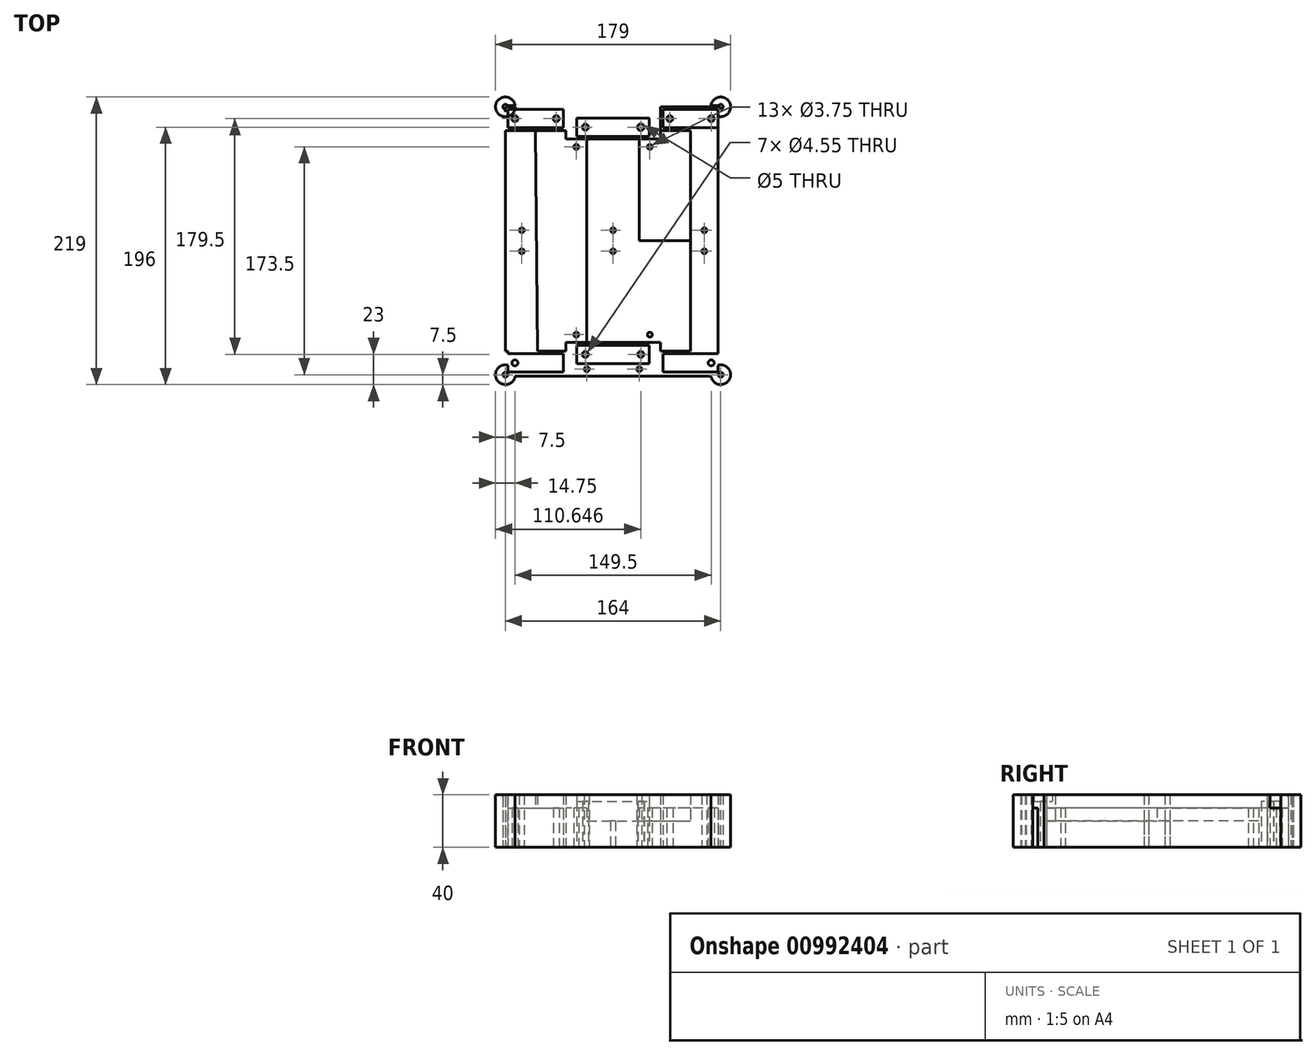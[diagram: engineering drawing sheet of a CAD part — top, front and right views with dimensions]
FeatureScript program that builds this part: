
annotation { "Feature Type Name" : "Feature", "Feature Type Description" : "" }
export const myFeature = defineFeature(function(context is Context, id is Id, definition is map)
    precondition{}
    {
        {
            var Q0;
            Q0=qCreatedBy(makeId("Top.planeOp"),FACE);
            var sketch = newSketch(context, id + "F0", { "sketchPlane" : qUnion([Q0])});
            skLineSegment(sketch, "E0.left", {"start": v(80, -100) * mm, "end": v(80, 100) * mm});
            skLineSegment(sketch, "E0.right", {"start": v(-80, -100) * mm, "end": v(-80, 100) * mm});
            skLineSegment(sketch, "E1.bottom", {"start": v(80, 100) * mm, "end": v(38, 100) * mm});
            skLineSegment(sketch, "E1.top", {"start": v(80, 86) * mm, "end": v(38, 86) * mm});
            skLineSegment(sketch, "E1.left", {"start": v(80, 100) * mm, "end": v(80, 86) * mm});
            skLineSegment(sketch, "E1.right", {"start": v(38, 100) * mm, "end": v(38, 86) * mm});
            skLineSegment(sketch, "E2.bottom", {"start": v(-80, 100) * mm, "end": v(-38, 100) * mm});
            skLineSegment(sketch, "E2.top", {"start": v(-80, 86) * mm, "end": v(-38, 86) * mm});
            skLineSegment(sketch, "E2.left", {"start": v(-80, 100) * mm, "end": v(-80, 86) * mm});
            skLineSegment(sketch, "E2.right", {"start": v(-38, 100) * mm, "end": v(-38, 86) * mm});
            skLineSegment(sketch, "E3.bottom", {"start": v(-27.6, 93.5) * mm, "end": v(27.65, 93.5) * mm});
            skLineSegment(sketch, "E3.top", {"start": v(-27.6, 79.5) * mm, "end": v(27.65, 79.5) * mm});
            skLineSegment(sketch, "E3.left", {"start": v(-27.6, 93.5) * mm, "end": v(-27.6, 79.5) * mm});
            skLineSegment(sketch, "E3.right", {"start": v(27.65, 93.5) * mm, "end": v(27.65, 79.5) * mm});
            skCircle(sketch, "E4", {"center": v(43.25, 93) * mm, "radius": 2.27 * mm});
            skPoint(sketch, "E4.centerSnap0", {"position": v(38, 93) * mm});
            skCircle(sketch, "E5", {"center": v(74.75, 93) * mm, "radius": 2.27 * mm});
            skCircle(sketch, "E6", {"center": v(-43.25, 93) * mm, "radius": 2.27 * mm});
            skPoint(sketch, "E6.centerSnap0", {"position": v(-38, 93) * mm});
            skCircle(sketch, "E7", {"center": v(-74.75, 93) * mm, "radius": 2.27 * mm});
            skPoint(sketch, "E7.centerSnap0", {"position": v(-80, 93) * mm});
            skCircle(sketch, "E8", {"center": v(-21.1, 86.5) * mm, "radius": 2.27 * mm});
            skPoint(sketch, "E8.centerSnap0", {"position": v(-27.6, 86.5) * mm});
            skCircle(sketch, "E9", {"center": v(21.15, 86.5) * mm, "radius": 2.5 * mm});
            skPoint(sketch, "E9.centerSnap0", {"position": v(27.65, 86.5) * mm});
            skLineSegment(sketch, "E10.2", {"start": v(-20, 77.5) * mm, "end": v(20, 77.5) * mm});
            skLineSegment(sketch, "E11.0", {"start": v(82, 102) * mm, "end": v(-82, 102) * mm});
            skLineSegment(sketch, "E11.1", {"start": v(82, -102) * mm, "end": v(82, 102) * mm});
            skLineSegment(sketch, "E11.3", {"start": v(-82, -102.02) * mm, "end": v(-82, 102) * mm});
            skLineSegment(sketch, "E12.0", {"start": v(-82, 84) * mm, "end": v(-36, 84) * mm});
            skLineSegment(sketch, "E12.1", {"start": v(-36, 102) * mm, "end": v(-36, 84) * mm});
            skLineSegment(sketch, "E13.0", {"start": v(82, 84) * mm, "end": v(36, 84) * mm});
            skLineSegment(sketch, "E13.1", {"start": v(36, 102) * mm, "end": v(36, 84) * mm});
            skLineSegment(sketch, "E14", {"start": v(-59, 84) * mm, "end": v(-57.51, -84) * mm});
            skLineSegment(sketch, "E15", {"start": v(59, 84) * mm, "end": v(59, -84) * mm});
            skLineSegment(sketch, "E16", {"start": v(82, 0) * mm, "end": v(80, 0) * mm});
            skLineSegment(sketch, "E17", {"start": v(80, 0) * mm, "end": v(59, 0) * mm});
            skLineSegment(sketch, "E18", {"start": v(59, 0) * mm, "end": v(0, 0) * mm});
            skLineSegment(sketch, "E19", {"start": v(0, 0) * mm, "end": v(-20, 0) * mm});
            skLineSegment(sketch, "E20", {"start": v(-58.26, 0) * mm, "end": v(-80, 0) * mm});
            skLineSegment(sketch, "E21.MirrorCS", {"start": v(-27.6, -93.5) * mm, "end": v(-27.6, -79.5) * mm});
            skCircle(sketch, "E22.MirrorC", {"center": v(-21.1, -86.5) * mm, "radius": 2.27 * mm});
            skCircle(sketch, "E23.MirrorC", {"center": v(74.75, -93) * mm, "radius": 2.27 * mm});
            skCircle(sketch, "E24.MirrorC", {"center": v(-74.75, -93) * mm, "radius": 2.27 * mm});
            skLineSegment(sketch, "E25.MirrorCS", {"start": v(-38, -100) * mm, "end": v(-38, -86) * mm});
            skLineSegment(sketch, "E26.MirrorCS", {"start": v(-36, -102) * mm, "end": v(-36, -84) * mm});
            skCircle(sketch, "E27.MirrorC", {"center": v(43.25, -93) * mm, "radius": 2.27 * mm});
            skCircle(sketch, "E28.MirrorC", {"center": v(21.15, -86.5) * mm, "radius": 2.27 * mm});
            skCircle(sketch, "E29.MirrorC", {"center": v(-43.25, -93) * mm, "radius": 2.27 * mm});
            skLineSegment(sketch, "E30.MirrorCS", {"start": v(27.65, -93.5) * mm, "end": v(27.65, -79.5) * mm});
            skLineSegment(sketch, "E31.MirrorCS", {"start": v(38, -100) * mm, "end": v(38, -86) * mm});
            skPoint(sketch, "E32.MirrorP", {"position": v(-38, -93) * mm});
            skLineSegment(sketch, "E33.MirrorCS", {"start": v(36, -102) * mm, "end": v(36, -84) * mm});
            skLineSegment(sketch, "E34.MirrorCS", {"start": v(80, -100) * mm, "end": v(80, -86) * mm});
            skPoint(sketch, "E35.MirrorP", {"position": v(-27.6, -86.5) * mm});
            skLineSegment(sketch, "E36.MirrorCS", {"start": v(-80, -100) * mm, "end": v(-80, -86) * mm});
            skLineSegment(sketch, "E37.MirrorCS", {"start": v(-82, -84) * mm, "end": v(-36, -84) * mm});
            skLineSegment(sketch, "E38.MirrorCS", {"start": v(-80, -86) * mm, "end": v(-38, -86) * mm});
            skPoint(sketch, "E39.MirrorP", {"position": v(38, -93) * mm});
            skLineSegment(sketch, "E40.MirrorCS", {"start": v(80, -86) * mm, "end": v(38, -86) * mm});
            skLineSegment(sketch, "E41.MirrorCS", {"start": v(-27.6, -79.5) * mm, "end": v(27.65, -79.5) * mm});
            skLineSegment(sketch, "E42.MirrorCS", {"start": v(82, -102.97) * mm, "end": v(-82, -102.97) * mm});
            skLineSegment(sketch, "E43.MirrorCS", {"start": v(82, -84) * mm, "end": v(36, -84) * mm});
            skPoint(sketch, "E44.MirrorP", {"position": v(27.65, -86.5) * mm});
            skLineSegment(sketch, "E45.MirrorCS", {"start": v(-27.6, -93.5) * mm, "end": v(27.65, -93.5) * mm});
            skLineSegment(sketch, "E46.MirrorCS", {"start": v(80, -100) * mm, "end": v(38, -100) * mm});
            skPoint(sketch, "E47.MirrorP", {"position": v(-80, -93) * mm});
            skLineSegment(sketch, "E48.MirrorCS", {"start": v(-80, -100) * mm, "end": v(-38, -100) * mm});
            skPoint(sketch, "E49", {"position": v(-80, 0) * mm});
            skPoint(sketch, "E50", {"position": v(-82, 0) * mm});
            skPoint(sketch, "E51", {"position": v(-80, 84) * mm});
            skPoint(sketch, "E52", {"position": v(-82, 84) * mm});
            skPoint(sketch, "E53", {"position": v(80, 84) * mm});
            skPoint(sketch, "E54", {"position": v(82, 84) * mm});
            skPoint(sketch, "E55", {"position": v(80, 0) * mm});
            skPoint(sketch, "E56", {"position": v(82, 0) * mm});
            skLineSegment(sketch, "E57", {"start": v(-82, 84) * mm, "end": v(-80, 84) * mm});
            skLineSegment(sketch, "E58", {"start": v(80, 84) * mm, "end": v(82, 84) * mm});
            skLineSegment(sketch, "E59", {"start": v(36, 102) * mm, "end": v(36, 100) * mm});
            skLineSegment(sketch, "E60", {"start": v(-82, 0) * mm, "end": v(-80, 0) * mm});
            skLineSegment(sketch, "E61", {"start": v(-82, -84) * mm, "end": v(-80, -84) * mm});
            skLineSegment(sketch, "E62", {"start": v(80, -84) * mm, "end": v(82, -84) * mm});
            skLineSegment(sketch, "E63", {"start": v(80, 0) * mm, "end": v(82, 0) * mm});
            skLineSegment(sketch, "E64", {"start": v(-38, 100) * mm, "end": v(-80, 100) * mm});
            skLineSegment(sketch, "E65", {"start": v(-57.51, -84) * mm, "end": v(-58.26, 0) * mm});
            skLineSegment(sketch, "E66", {"start": v(-58.26, 0) * mm, "end": v(-20, 0) * mm});
            skCircle(sketch, "E67.MirrorC", {"center": v(21.15, 86.5) * mm, "radius": 2.27 * mm});
            skLineSegment(sketch, "E68.MirrorCS", {"start": v(82, 102.97) * mm, "end": v(-82, 102.97) * mm});
            skLineSegment(sketch, "E69", {"start": v(36, -102) * mm, "end": v(36, -77.5) * mm});
            skLineSegment(sketch, "E70", {"start": v(-36, -102) * mm, "end": v(-36, -77.5) * mm});
            skLineSegment(sketch, "E71", {"start": v(36, -77.5) * mm, "end": v(-36, -77.5) * mm});
            skLineSegment(sketch, "E72", {"start": v(20, -77.5) * mm, "end": v(20, 77.5) * mm});
            skLineSegment(sketch, "E73", {"start": v(-20, 77.5) * mm, "end": v(-20, -77.5) * mm});
            skLineSegment(sketch, "E74", {"start": v(36, 84) * mm, "end": v(36, 77.5) * mm});
            skLineSegment(sketch, "E75", {"start": v(36, 77.5) * mm, "end": v(20, 77.5) * mm});
            skLineSegment(sketch, "E76", {"start": v(-36, 84) * mm, "end": v(-36, 77.5) * mm});
            skLineSegment(sketch, "E77", {"start": v(-20, 77.5) * mm, "end": v(-36, 77.5) * mm});
            skLineSegment(sketch, "E78.bottom", {"start": v(-36, 102) * mm, "end": v(36, 102) * mm});
            skLineSegment(sketch, "E78.top", {"start": v(-36, 172) * mm, "end": v(36, 172) * mm});
            skLineSegment(sketch, "E78.left", {"start": v(-36, 102) * mm, "end": v(-36, 172) * mm});
            skLineSegment(sketch, "E78.right", {"start": v(36, 102) * mm, "end": v(36, 172) * mm});
            skLineSegment(sketch, "E79", {"start": v(0, 102) * mm, "end": v(0, 172) * mm});
            skCircle(sketch, "E80", {"center": v(-15, 127) * mm, "radius": 2 * mm});
            skCircle(sketch, "E81", {"center": v(-15, 152.4) * mm, "radius": 2 * mm});
            skCircle(sketch, "E82.MirrorC", {"center": v(15, 127) * mm, "radius": 2 * mm});
            skCircle(sketch, "E83.MirrorC", {"center": v(15, 152.4) * mm, "radius": 2 * mm});
            skLineSegment(sketch, "E84", {"start": v(-33.47, 102) * mm, "end": v(-33.47, 98) * mm});
            skLineSegment(sketch, "E85", {"start": v(-33.47, 98) * mm, "end": v(-29.47, 98) * mm});
            skLineSegment(sketch, "E86", {"start": v(-29.47, 98) * mm, "end": v(-29.47, 100) * mm});
            skLineSegment(sketch, "E87", {"start": v(-29.47, 100) * mm, "end": v(-31.47, 100) * mm});
            skLineSegment(sketch, "E88", {"start": v(-31.47, 100) * mm, "end": v(-31.47, 102) * mm});
            skLineSegment(sketch, "E89.0", {"start": v(-31.27, 100.2) * mm, "end": v(-31.27, 102) * mm});
            skLineSegment(sketch, "E89.1", {"start": v(-33.67, 102) * mm, "end": v(-33.67, 97.8) * mm});
            skLineSegment(sketch, "E89.2", {"start": v(-33.67, 97.8) * mm, "end": v(-29.27, 97.8) * mm});
            skLineSegment(sketch, "E89.3", {"start": v(-29.27, 97.8) * mm, "end": v(-29.27, 100.2) * mm});
            skLineSegment(sketch, "E89.4", {"start": v(-29.27, 100.2) * mm, "end": v(-31.27, 100.2) * mm});
            skLineSegment(sketch, "E90.MirrorCS", {"start": v(31.27, 100.2) * mm, "end": v(31.27, 102) * mm});
            skLineSegment(sketch, "E91.MirrorCS", {"start": v(31.47, 100) * mm, "end": v(31.47, 102) * mm});
            skLineSegment(sketch, "E92.MirrorCS", {"start": v(33.47, 102) * mm, "end": v(33.47, 98) * mm});
            skLineSegment(sketch, "E93.MirrorCS", {"start": v(33.67, 102) * mm, "end": v(33.67, 97.8) * mm});
            skLineSegment(sketch, "E94.MirrorCS", {"start": v(29.27, 97.8) * mm, "end": v(29.27, 100.2) * mm});
            skLineSegment(sketch, "E95.MirrorCS", {"start": v(29.47, 100) * mm, "end": v(31.47, 100) * mm});
            skLineSegment(sketch, "E96.MirrorCS", {"start": v(33.67, 97.8) * mm, "end": v(29.27, 97.8) * mm});
            skLineSegment(sketch, "E97.MirrorCS", {"start": v(29.47, 98) * mm, "end": v(29.47, 100) * mm});
            skLineSegment(sketch, "E98.MirrorCS", {"start": v(29.27, 100.2) * mm, "end": v(31.27, 100.2) * mm});
            skLineSegment(sketch, "E99.MirrorCS", {"start": v(33.47, 98) * mm, "end": v(29.47, 98) * mm});
            skLineSegment(sketch, "E100", {"start": v(-39.13, 0) * mm, "end": v(-39.13, -2.14) * mm});
            skLineSegment(sketch, "E101", {"start": v(-39.13, -2.14) * mm, "end": v(-37.13, -2.14) * mm});
            skLineSegment(sketch, "E102", {"start": v(-37.13, -2.14) * mm, "end": v(-37.13, -4.14) * mm});
            skLineSegment(sketch, "E103", {"start": v(-37.13, -4.14) * mm, "end": v(-43.13, -4.14) * mm});
            skLineSegment(sketch, "E104", {"start": v(-43.13, -4.14) * mm, "end": v(-43.13, -2.14) * mm});
            skLineSegment(sketch, "E105", {"start": v(-43.13, -2.14) * mm, "end": v(-41.13, -2.15) * mm});
            skLineSegment(sketch, "E106", {"start": v(-41.13, -2.15) * mm, "end": v(-41.13, 0) * mm});
            skLineSegment(sketch, "E107.0", {"start": v(-41.38, -1.9) * mm, "end": v(-41.38, 0) * mm});
            skLineSegment(sketch, "E107.1", {"start": v(-43.38, -1.89) * mm, "end": v(-41.38, -1.9) * mm});
            skLineSegment(sketch, "E107.2", {"start": v(-43.38, -4.39) * mm, "end": v(-43.38, -1.89) * mm});
            skLineSegment(sketch, "E107.3", {"start": v(-38.88, 0) * mm, "end": v(-38.88, -1.89) * mm});
            skLineSegment(sketch, "E107.4", {"start": v(-38.88, -1.89) * mm, "end": v(-36.88, -1.89) * mm});
            skLineSegment(sketch, "E107.5", {"start": v(-36.88, -1.89) * mm, "end": v(-36.88, -4.39) * mm});
            skLineSegment(sketch, "E107.6", {"start": v(-36.88, -4.39) * mm, "end": v(-43.38, -4.39) * mm});
            skLineSegment(sketch, "E108.MirrorCS", {"start": v(43.13, -2.14) * mm, "end": v(41.13, -2.15) * mm});
            skLineSegment(sketch, "E109.MirrorCS", {"start": v(39.13, -2.14) * mm, "end": v(37.13, -2.14) * mm});
            skLineSegment(sketch, "E110.MirrorCS", {"start": v(36.88, -4.39) * mm, "end": v(43.38, -4.39) * mm});
            skLineSegment(sketch, "E111.MirrorCS", {"start": v(43.38, -1.89) * mm, "end": v(41.38, -1.9) * mm});
            skLineSegment(sketch, "E112.MirrorCS", {"start": v(37.13, -4.14) * mm, "end": v(43.13, -4.14) * mm});
            skLineSegment(sketch, "E113.MirrorCS", {"start": v(36.88, -1.89) * mm, "end": v(36.88, -4.39) * mm});
            skLineSegment(sketch, "E114.MirrorCS", {"start": v(43.38, -4.39) * mm, "end": v(43.38, -1.89) * mm});
            skLineSegment(sketch, "E115.MirrorCS", {"start": v(38.88, -1.89) * mm, "end": v(36.88, -1.89) * mm});
            skLineSegment(sketch, "E116.MirrorCS", {"start": v(43.13, -4.14) * mm, "end": v(43.13, -2.14) * mm});
            skLineSegment(sketch, "E117.MirrorCS", {"start": v(37.13, -2.14) * mm, "end": v(37.13, -4.14) * mm});
            skLineSegment(sketch, "E118.MirrorCS", {"start": v(41.38, -1.9) * mm, "end": v(41.38, 0) * mm});
            skLineSegment(sketch, "E119.MirrorCS", {"start": v(41.13, -2.15) * mm, "end": v(41.13, 0) * mm});
            skLineSegment(sketch, "E120.MirrorCS", {"start": v(39.13, 0) * mm, "end": v(39.13, -2.14) * mm});
            skLineSegment(sketch, "E121.MirrorCS", {"start": v(38.88, 0) * mm, "end": v(38.88, -1.89) * mm});
            skLineSegment(sketch, "E122.MirrorCS", {"start": v(-29.27, -100.2) * mm, "end": v(-31.27, -100.2) * mm});
            skLineSegment(sketch, "E123.MirrorCS", {"start": v(-29.27, -97.8) * mm, "end": v(-29.27, -100.2) * mm});
            skLineSegment(sketch, "E124.MirrorCS", {"start": v(-33.47, -98) * mm, "end": v(-29.47, -98) * mm});
            skLineSegment(sketch, "E125.MirrorCS", {"start": v(-29.47, -100) * mm, "end": v(-31.47, -100) * mm});
            skLineSegment(sketch, "E126.MirrorCS", {"start": v(-29.47, -98) * mm, "end": v(-29.47, -100) * mm});
            skLineSegment(sketch, "E127.MirrorCS", {"start": v(-33.67, -97.8) * mm, "end": v(-29.27, -97.8) * mm});
            skLineSegment(sketch, "E128.MirrorCS", {"start": v(-33.67, -102) * mm, "end": v(-33.67, -97.8) * mm});
            skLineSegment(sketch, "E129.MirrorCS", {"start": v(-33.47, -102) * mm, "end": v(-33.47, -98) * mm});
            skLineSegment(sketch, "E130.MirrorCS", {"start": v(-31.47, -100) * mm, "end": v(-31.47, -102) * mm});
            skLineSegment(sketch, "E131.MirrorCS", {"start": v(-31.27, -100.2) * mm, "end": v(-31.27, -102) * mm});
            skLineSegment(sketch, "E132.MirrorCS", {"start": v(29.27, -97.8) * mm, "end": v(29.27, -100.2) * mm});
            skLineSegment(sketch, "E133.MirrorCS", {"start": v(29.27, -100.2) * mm, "end": v(31.27, -100.2) * mm});
            skLineSegment(sketch, "E134.MirrorCS", {"start": v(29.47, -98) * mm, "end": v(29.47, -100) * mm});
            skLineSegment(sketch, "E135.MirrorCS", {"start": v(29.47, -100) * mm, "end": v(31.47, -100) * mm});
            skLineSegment(sketch, "E136.MirrorCS", {"start": v(33.67, -97.8) * mm, "end": v(29.27, -97.8) * mm});
            skLineSegment(sketch, "E137.MirrorCS", {"start": v(33.47, -98) * mm, "end": v(29.47, -98) * mm});
            skLineSegment(sketch, "E138.MirrorCS", {"start": v(33.47, -102) * mm, "end": v(33.47, -98) * mm});
            skLineSegment(sketch, "E139.MirrorCS", {"start": v(33.67, -102) * mm, "end": v(33.67, -97.8) * mm});
            skLineSegment(sketch, "E140.MirrorCS", {"start": v(31.47, -100) * mm, "end": v(31.47, -102) * mm});
            skLineSegment(sketch, "E141.MirrorCS", {"start": v(31.27, -100.2) * mm, "end": v(31.27, -102) * mm});
            skCircle(sketch, "E142", {"center": v(36, 172) * mm, "radius": 7.5 * mm});
            skCircle(sketch, "E143.MirrorC", {"center": v(-36, 172) * mm, "radius": 7.5 * mm});
            skCircle(sketch, "E144", {"center": v(82, 102) * mm, "radius": 7.5 * mm});
            skCircle(sketch, "E145", {"center": v(82, -102) * mm, "radius": 7.5 * mm});
            skCircle(sketch, "E146", {"center": v(82, -102) * mm, "radius": 1.88 * mm});
            skCircle(sketch, "E147", {"center": v(82, 102) * mm, "radius": 1.88 * mm});
            skCircle(sketch, "E148", {"center": v(36, 172) * mm, "radius": 1.88 * mm});
            skCircle(sketch, "E149.MirrorC", {"center": v(-36, 172) * mm, "radius": 1.88 * mm});
            skCircle(sketch, "E150.MirrorC", {"center": v(-82, 102) * mm, "radius": 1.88 * mm});
            skCircle(sketch, "E151.MirrorC", {"center": v(-82, 102) * mm, "radius": 7.5 * mm});
            skCircle(sketch, "E152.MirrorC", {"center": v(-82, -102) * mm, "radius": 1.88 * mm});
            skCircle(sketch, "E153.MirrorC", {"center": v(-82, -102) * mm, "radius": 7.5 * mm});
            skCircle(sketch, "E154", {"center": v(24, 108) * mm, "radius": 1.88 * mm});
            skCircle(sketch, "E155.MirrorC", {"center": v(-24, 108) * mm, "radius": 1.88 * mm});
            skCircle(sketch, "E156", {"center": v(20, 97.8) * mm, "radius": 1.88 * mm});
            skLineSegment(sketch, "E157", {"start": v(0, 102) * mm, "end": v(0, 93.5) * mm});
            skPoint(sketch, "E158", {"position": v(0, 97.75) * mm});
            skCircle(sketch, "E159.MirrorC", {"center": v(-20, 97.8) * mm, "radius": 1.88 * mm});
            skCircle(sketch, "E160.MirrorC", {"center": v(-20, -97.8) * mm, "radius": 1.88 * mm});
            skCircle(sketch, "E161.MirrorC", {"center": v(20, -97.8) * mm, "radius": 1.88 * mm});
            skCircle(sketch, "E162", {"center": v(0, -8) * mm, "radius": 1.88 * mm});
            skCircle(sketch, "E163", {"center": v(69.5, -8) * mm, "radius": 1.88 * mm});
            skPoint(sketch, "E163.centerSnap0", {"position": v(69.5, 0) * mm});
            skCircle(sketch, "E164.MirrorC", {"center": v(-69.5, -8) * mm, "radius": 1.88 * mm});
            skCircle(sketch, "E165.MirrorC", {"center": v(-69.5, 8) * mm, "radius": 1.88 * mm});
            skCircle(sketch, "E166.MirrorC", {"center": v(0, 8) * mm, "radius": 1.88 * mm});
            skCircle(sketch, "E167.MirrorC", {"center": v(69.5, 8) * mm, "radius": 1.88 * mm});
            skCircle(sketch, "E168", {"center": v(28, 71.5) * mm, "radius": 1.88 * mm});
            skCircle(sketch, "E169.MirrorC", {"center": v(-28, 71.5) * mm, "radius": 1.88 * mm});
            skCircle(sketch, "E170.MirrorC", {"center": v(28, -71.5) * mm, "radius": 1.88 * mm});
            skCircle(sketch, "E171.MirrorC", {"center": v(-28, -71.5) * mm, "radius": 1.88 * mm});
            skPoint(sketch, "E172", {"position": v(0, -102.97) * mm});
            skLineSegment(sketch, "E173", {"start": v(0, -102.97) * mm, "end": v(0, -166.97) * mm});
            skLineSegment(sketch, "E174.bottom", {"start": v(59.56, -102.97) * mm, "end": v(-59.56, -102.97) * mm});
            skPoint(sketch, "E174.middle", {"position": v(0, -166.97) * mm});
            skLineSegment(sketch, "E175", {"start": v(-59.56, -166.97) * mm, "end": v(59.56, -166.97) * mm});
            skLineSegment(sketch, "E176.0", {"start": v(-59.56, -162.97) * mm, "end": v(59.56, -162.97) * mm});
            skLineSegment(sketch, "E177", {"start": v(-59.56, -102.97) * mm, "end": v(-59.56, -166.97) * mm});
            skLineSegment(sketch, "E178", {"start": v(59.56, -102.97) * mm, "end": v(59.56, -166.97) * mm});
            skLineSegment(sketch, "E179", {"start": v(-59.56, -166.97) * mm, "end": v(-59.56, -316.97) * mm});
            skLineSegment(sketch, "E180", {"start": v(-59.56, -316.97) * mm, "end": v(59.56, -316.97) * mm});
            skLineSegment(sketch, "E181", {"start": v(59.56, -316.97) * mm, "end": v(59.56, -166.97) * mm});
            skSolve(sketch);
        }
        {
            var Q0;
            {var subQ4=sQuery(id+"F0.wireOp",EDGE,"E14");Q0=makeQuery(id+"F0.imprint","IMPRINT",FACE,{"disambiguationData":[TD([[makeQuery(id+"F0.imprint","IMPRINT",EDGE,{"derivedFrom":subQ4}),-1.0]])]});}
            var Q1;
            {var subQ4=sQuery(id+"F0.wireOp",EDGE,"E19");Q1=makeQuery(id+"F0.imprint","IMPRINT",FACE,{"disambiguationData":[TD([[makeQuery(id+"F0.imprint","IMPRINT",EDGE,{"derivedFrom":subQ4}),-1.0]])]});}
            var Q2;
            Q2=makeQuery(id+"F0.imprint","IMPRINT",FACE,{"disambiguationData":[TD([[makeQuery(id+"F0.imprint","IMPRINT",EDGE,{"derivedFrom":sQuery(id+"F0.wireOp",EDGE,"E21.MirrorCS")}),-1.0]])]});
            var Q3;
            Q3=makeQuery(id+"F0.imprint","IMPRINT",FACE,{"disambiguationData":[TD([[makeQuery(id+"F0.imprint","IMPRINT",EDGE,{"derivedFrom":sQuery(id+"F0.wireOp",EDGE,"E23.MirrorC")}),1.0]])]});
            var Q4;
            {var subQ6=sQuery(id+"F0.wireOp",EDGE,"E74");Q4=makeQuery(id+"F0.imprint","IMPRINT",FACE,{"disambiguationData":[TD([[makeQuery(id+"F0.imprint","IMPRINT",EDGE,{"derivedFrom":subQ6}),1.0]])]});}
            var Q5;
            Q5=makeQuery(id+"F0.imprint","IMPRINT",FACE,{"disambiguationData":[TD([[makeQuery(id+"F0.imprint","IMPRINT",EDGE,{"derivedFrom":sQuery(id+"F0.wireOp",EDGE,"E24.MirrorC")}),1.0]])]});
            var Q6;
            {var subQ1=sQuery(id+"F0.wireOp",EDGE,"E43.MirrorCS");var subQ6=sQuery(id+"F0.wireOp",EDGE,"E15");var subQ10=makeQuery(id+"F0.imprint","INTERSECT",VERTEX,{"derivedFrom":[subQ6,subQ1]});Q6=makeQuery(id+"F0.imprint","IMPRINT",FACE,{"disambiguationData":[TD([[makeQuery(id+"F0.imprint","IMPRINT",EDGE,{"disambiguationData":[TD([[subQ10,-1.0]])],"derivedFrom":subQ1}),-1.0]])]});}
            var Q7;
            Q7=makeQuery(id+"F0.imprint","IMPRINT",FACE,{"disambiguationData":[TD([[makeQuery(id+"F0.imprint","IMPRINT",EDGE,{"derivedFrom":sQuery(id+"F0.wireOp",EDGE,"E7")}),-1.0]])]});
            var Q8;
            {var subQ7=sQuery(id+"F0.wireOp",EDGE,"E19");Q8=makeQuery(id+"F0.imprint","IMPRINT",FACE,{"disambiguationData":[TD([[makeQuery(id+"F0.imprint","IMPRINT",EDGE,{"derivedFrom":subQ7}),1.0]])]});}
            var Q9;
            Q9=makeQuery(id+"F0.imprint","IMPRINT",FACE,{"disambiguationData":[TD([[makeQuery(id+"F0.imprint","IMPRINT",EDGE,{"derivedFrom":sQuery(id+"F0.wireOp",EDGE,"E1.right")}),1.0]])]});
            var Q10;
            {var subQ6=sQuery(id+"F0.wireOp",EDGE,"E65");Q10=makeQuery(id+"F0.imprint","IMPRINT",FACE,{"disambiguationData":[TD([[makeQuery(id+"F0.imprint","IMPRINT",EDGE,{"derivedFrom":subQ6}),-1.0]])]});}
            var Q11;
            Q11=makeQuery(id+"F0.imprint","IMPRINT",FACE,{"disambiguationData":[TD([[makeQuery(id+"F0.imprint","IMPRINT",EDGE,{"derivedFrom":sQuery(id+"F0.wireOp",EDGE,"E8")}),-1.0]])]});
            var Q12;
            {var subQ1=sQuery(id+"F0.wireOp",EDGE,"E14");Q12=makeQuery(id+"F0.imprint","IMPRINT",FACE,{"disambiguationData":[TD([[makeQuery(id+"F0.imprint","IMPRINT",EDGE,{"derivedFrom":subQ1}),1.0]])]});}
            var Q13;
            {var subQ0=sQuery(id+"F0.wireOp",EDGE,"E17");Q13=makeQuery(id+"F0.imprint","IMPRINT",FACE,{"disambiguationData":[TD([[makeQuery(id+"F0.imprint","IMPRINT",EDGE,{"derivedFrom":subQ0}),1.0]])]});}
            var Q14;
            Q14=makeQuery(id+"F0.imprint","IMPRINT",FACE,{"disambiguationData":[TD([[makeQuery(id+"F0.imprint","IMPRINT",EDGE,{"derivedFrom":sQuery(id+"F0.wireOp",EDGE,"E21.MirrorCS")}),1.0]])]});
            var Q15;
            {var subQ0=sQuery(id+"F0.wireOp",EDGE,"E17");Q15=makeQuery(id+"F0.imprint","IMPRINT",FACE,{"disambiguationData":[TD([[makeQuery(id+"F0.imprint","IMPRINT",EDGE,{"derivedFrom":subQ0}),-1.0]])]});}
            var Q16;
            {var subQ6=sQuery(id+"F0.wireOp",EDGE,"E12.1");Q16=makeQuery(id+"F0.imprint","IMPRINT",FACE,{"disambiguationData":[TD([[makeQuery(id+"F0.imprint","IMPRINT",EDGE,{"derivedFrom":subQ6}),1.0]])]});}
            var Q17;
            {var subQ0=sQuery(id+"F0.wireOp",EDGE,"E20");Q17=makeQuery(id+"F0.imprint","IMPRINT",FACE,{"disambiguationData":[TD([[makeQuery(id+"F0.imprint","IMPRINT",EDGE,{"derivedFrom":subQ0}),1.0]])]});}
            var Q18;
            {var subQ2=sQuery(id+"F0.wireOp",EDGE,"E62");Q18=makeQuery(id+"F0.imprint","IMPRINT",FACE,{"disambiguationData":[TD([[makeQuery(id+"F0.imprint","IMPRINT",EDGE,{"derivedFrom":subQ2}),1.0]])]});}
            var Q19;
            {var subQ0=sQuery(id+"F0.wireOp",EDGE,"E63");Q19=makeQuery(id+"F0.imprint","IMPRINT",FACE,{"disambiguationData":[TD([[makeQuery(id+"F0.imprint","IMPRINT",EDGE,{"derivedFrom":subQ0}),1.0]])]});}
            var Q20;
            Q20=makeQuery(id+"F0.imprint","IMPRINT",FACE,{"disambiguationData":[TD([[makeQuery(id+"F0.imprint","IMPRINT",EDGE,{"derivedFrom":sQuery(id+"F0.wireOp",EDGE,"E31.MirrorCS")}),1.0]])]});
            var Q21;
            {var subQ0=sQuery(id+"F0.wireOp",EDGE,"E60");Q21=makeQuery(id+"F0.imprint","IMPRINT",FACE,{"disambiguationData":[TD([[makeQuery(id+"F0.imprint","IMPRINT",EDGE,{"derivedFrom":subQ0}),-1.0]])]});}
            var Q22;
            {var subQ0=sQuery(id+"F0.wireOp",EDGE,"E60");Q22=makeQuery(id+"F0.imprint","IMPRINT",FACE,{"disambiguationData":[TD([[makeQuery(id+"F0.imprint","IMPRINT",EDGE,{"derivedFrom":subQ0}),1.0]])]});}
            var Q23;
            Q23=makeQuery(id+"F0.imprint","IMPRINT",FACE,{"disambiguationData":[TD([[makeQuery(id+"F0.imprint","IMPRINT",EDGE,{"derivedFrom":sQuery(id+"F0.wireOp",EDGE,"E25.MirrorCS")}),-1.0]])]});
            var Q24;
            Q24=makeQuery(id+"F0.imprint","IMPRINT",FACE,{"disambiguationData":[TD([[makeQuery(id+"F0.imprint","IMPRINT",EDGE,{"derivedFrom":sQuery(id+"F0.wireOp",EDGE,"E1.right")}),-1.0]])]});
            var Q25;
            {var subQ3=sQuery(id+"F0.wireOp",EDGE,"E12.1");Q25=makeQuery(id+"F0.imprint","IMPRINT",FACE,{"disambiguationData":[TD([[makeQuery(id+"F0.imprint","IMPRINT",EDGE,{"derivedFrom":subQ3}),-1.0]])]});}
            var Q26;
            {var subQ0=sQuery(id+"F0.wireOp",EDGE,"E144");var subQ1=sQuery(id+"F0.wireOp",EDGE,"E11.1");var subQ2=makeQuery(id+"F0.imprint","INTERSECT",VERTEX,{"derivedFrom":[subQ1,subQ0]});Q26=makeQuery(id+"F0.imprint","IMPRINT",FACE,{"disambiguationData":[TD([[makeQuery(id+"F0.imprint","IMPRINT",EDGE,{"disambiguationData":[TD([[subQ2,-1.0]])],"derivedFrom":subQ1}),-1.0]])]});}
            var Q27;
            {var subQ5=sQuery(id+"F0.wireOp",EDGE,"E13.0");var subQ6=sQuery(id+"F0.wireOp",EDGE,"E11.1");var subQ7=makeQuery(id+"F0.imprint","INTERSECT",VERTEX,{"derivedFrom":[subQ6,subQ5]});Q27=makeQuery(id+"F0.imprint","IMPRINT",FACE,{"disambiguationData":[TD([[makeQuery(id+"F0.imprint","IMPRINT",EDGE,{"disambiguationData":[TD([[subQ7,-1.0]])],"derivedFrom":subQ6}),1.0]])]});}
            var Q28;
            {var subQ3=sQuery(id+"F0.wireOp",EDGE,"E144");var subQ10=sQuery(id+"F0.wireOp",EDGE,"E11.1");var subQ11=makeQuery(id+"F0.imprint","INTERSECT",VERTEX,{"derivedFrom":[subQ10,subQ3]});Q28=makeQuery(id+"F0.imprint","IMPRINT",FACE,{"disambiguationData":[TD([[makeQuery(id+"F0.imprint","IMPRINT",EDGE,{"disambiguationData":[TD([[subQ11,-1.0]])],"derivedFrom":subQ10}),1.0]])]});}
            var Q29;
            {var subQ0=sQuery(id+"F0.wireOp",EDGE,"E1.left");var subQ1=sQuery(id+"F0.wireOp",EDGE,"E1.bottom");var subQ2=makeQuery(id+"F0.imprint","INTERSECT",VERTEX,{"derivedFrom":[subQ1,subQ0]});Q29=makeQuery(id+"F0.imprint","IMPRINT",FACE,{"disambiguationData":[TD([[makeQuery(id+"F0.imprint","IMPRINT",EDGE,{"disambiguationData":[TD([[subQ2,-1.0]])],"derivedFrom":subQ1}),1.0]])]});}
            var Q30;
            {var subQ0=sQuery(id+"F0.wireOp",EDGE,"E12.0");var subQ1=sQuery(id+"F0.wireOp",EDGE,"E11.3");var subQ2=makeQuery(id+"F0.imprint","INTERSECT",VERTEX,{"derivedFrom":[subQ1,subQ0]});Q30=makeQuery(id+"F0.imprint","IMPRINT",FACE,{"disambiguationData":[TD([[makeQuery(id+"F0.imprint","IMPRINT",EDGE,{"disambiguationData":[TD([[subQ2,-1.0]])],"derivedFrom":subQ1}),-1.0]])]});}
            var Q31;
            {var subQ3=sQuery(id+"F0.wireOp",EDGE,"E151.MirrorC");var subQ7=sQuery(id+"F0.wireOp",EDGE,"E11.3");var subQ12=makeQuery(id+"F0.imprint","INTERSECT",VERTEX,{"derivedFrom":[subQ7,subQ3]});Q31=makeQuery(id+"F0.imprint","IMPRINT",FACE,{"disambiguationData":[TD([[makeQuery(id+"F0.imprint","IMPRINT",EDGE,{"disambiguationData":[TD([[subQ12,-1.0]])],"derivedFrom":subQ7}),-1.0]])]});}
            var Q32;
            {var subQ0=sQuery(id+"F0.wireOp",EDGE,"E151.MirrorC");var subQ1=sQuery(id+"F0.wireOp",EDGE,"E11.3");var subQ2=makeQuery(id+"F0.imprint","INTERSECT",VERTEX,{"derivedFrom":[subQ1,subQ0]});Q32=makeQuery(id+"F0.imprint","IMPRINT",FACE,{"disambiguationData":[TD([[makeQuery(id+"F0.imprint","IMPRINT",EDGE,{"disambiguationData":[TD([[subQ2,-1.0]])],"derivedFrom":subQ1}),1.0]])]});}
            var Q33;
            {var subQ0=sQuery(id+"F0.wireOp",EDGE,"E61");Q33=makeQuery(id+"F0.imprint","IMPRINT",FACE,{"disambiguationData":[TD([[makeQuery(id+"F0.imprint","IMPRINT",EDGE,{"derivedFrom":subQ0}),-1.0]])]});}
            var Q34;
            {var subQ3=sQuery(id+"F0.wireOp",EDGE,"E153.MirrorC");var subQ5=sQuery(id+"F0.wireOp",EDGE,"E11.3");var subQ6=makeQuery(id+"F0.imprint","INTERSECT",VERTEX,{"derivedFrom":[subQ5,subQ3]});Q34=makeQuery(id+"F0.imprint","IMPRINT",FACE,{"disambiguationData":[TD([[makeQuery(id+"F0.imprint","IMPRINT",EDGE,{"disambiguationData":[TD([[subQ6,1.0]])],"derivedFrom":subQ5}),-1.0]])]});}
            var Q35;
            {var subQ0=sQuery(id+"F0.wireOp",EDGE,"E153.MirrorC");var subQ1=sQuery(id+"F0.wireOp",EDGE,"E11.3");var subQ2=makeQuery(id+"F0.imprint","INTERSECT",VERTEX,{"derivedFrom":[subQ1,subQ0]});Q35=makeQuery(id+"F0.imprint","IMPRINT",FACE,{"disambiguationData":[TD([[makeQuery(id+"F0.imprint","IMPRINT",EDGE,{"disambiguationData":[TD([[subQ2,1.0]])],"derivedFrom":subQ1}),1.0]])]});}
            var Q36;
            {var subQ0=sQuery(id+"F0.wireOp",EDGE,"E48.MirrorCS");var subQ1=sQuery(id+"F0.wireOp",EDGE,"E36.MirrorCS");var subQ2=makeQuery(id+"F0.imprint","INTERSECT",VERTEX,{"derivedFrom":[subQ1,subQ0]});Q36=makeQuery(id+"F0.imprint","IMPRINT",FACE,{"disambiguationData":[TD([[makeQuery(id+"F0.imprint","IMPRINT",EDGE,{"disambiguationData":[TD([[subQ2,-1.0]])],"derivedFrom":subQ1}),-1.0]])]});}
            var Q37;
            {var subQ0=sQuery(id+"F0.wireOp",EDGE,"E2.bottom");var subQ1=sQuery(id+"F0.wireOp",EDGE,"E2.left");var subQ2=makeQuery(id+"F0.imprint","INTERSECT",VERTEX,{"derivedFrom":[subQ1,subQ0]});Q37=makeQuery(id+"F0.imprint","IMPRINT",FACE,{"disambiguationData":[TD([[makeQuery(id+"F0.imprint","IMPRINT",EDGE,{"disambiguationData":[TD([[subQ2,-1.0]])],"derivedFrom":subQ1}),1.0]])]});}
            var Q38;
            {var subQ0=sQuery(id+"F0.wireOp",EDGE,"E46.MirrorCS");var subQ1=sQuery(id+"F0.wireOp",EDGE,"E34.MirrorCS");var subQ2=makeQuery(id+"F0.imprint","INTERSECT",VERTEX,{"derivedFrom":[subQ1,subQ0]});Q38=makeQuery(id+"F0.imprint","IMPRINT",FACE,{"disambiguationData":[TD([[makeQuery(id+"F0.imprint","IMPRINT",EDGE,{"disambiguationData":[TD([[subQ2,-1.0]])],"derivedFrom":subQ1}),1.0]])]});}
            var Q39;
            {var subQ3=sQuery(id+"F0.wireOp",EDGE,"E145");var subQ10=sQuery(id+"F0.wireOp",EDGE,"E11.1");var subQ11=makeQuery(id+"F0.imprint","INTERSECT",VERTEX,{"derivedFrom":[subQ10,subQ3]});Q39=makeQuery(id+"F0.imprint","IMPRINT",FACE,{"disambiguationData":[TD([[makeQuery(id+"F0.imprint","IMPRINT",EDGE,{"disambiguationData":[TD([[subQ11,1.0]])],"derivedFrom":subQ10}),1.0]])]});}
            var Q40;
            {var subQ0=sQuery(id+"F0.wireOp",EDGE,"E62");Q40=makeQuery(id+"F0.imprint","IMPRINT",FACE,{"disambiguationData":[TD([[makeQuery(id+"F0.imprint","IMPRINT",EDGE,{"derivedFrom":subQ0}),-1.0]])]});}
            var Q41;
            {var subQ0=sQuery(id+"F0.wireOp",EDGE,"E145");var subQ1=sQuery(id+"F0.wireOp",EDGE,"E11.1");var subQ2=makeQuery(id+"F0.imprint","INTERSECT",VERTEX,{"derivedFrom":[subQ1,subQ0]});Q41=makeQuery(id+"F0.imprint","IMPRINT",FACE,{"disambiguationData":[TD([[makeQuery(id+"F0.imprint","IMPRINT",EDGE,{"disambiguationData":[TD([[subQ2,1.0]])],"derivedFrom":subQ1}),-1.0]])]});}
            var Q42;
            {var subQ0=sQuery(id+"F0.wireOp",EDGE,"E100");Q42=makeQuery(id+"F0.imprint","IMPRINT",FACE,{"disambiguationData":[TD([[makeQuery(id+"F0.imprint","IMPRINT",EDGE,{"derivedFrom":subQ0}),-1.0]])]});}
            var Q43;
            {var subQ7=sQuery(id+"F0.wireOp",EDGE,"E100");Q43=makeQuery(id+"F0.imprint","IMPRINT",FACE,{"disambiguationData":[TD([[makeQuery(id+"F0.imprint","IMPRINT",EDGE,{"derivedFrom":subQ7}),1.0]])]});}
            extrude(context, id + "F1", {"entities" : qUnion([Q0, Q1, Q2, Q3, Q4, Q5, Q6, Q7, Q8, Q9, Q10, Q11, Q12, Q13, Q14, Q15, Q16, Q17, Q18, Q19, Q20, Q21, Q22, Q23, Q24, Q25, Q26, Q27, Q28, Q29, Q30, Q31, Q32, Q33, Q34, Q35, Q36, Q37, Q38, Q39, Q40, Q41, Q42, Q43]), "depth" : 20 * mm, "offsetDistance" : 25 * mm});
        }
        {
            var Q0;
            {var subQ1=sQuery(id+"F0.wireOp",EDGE,"E1.right");Q0=makeQuery(id+"F0.imprint","IMPRINT",FACE,{"disambiguationData":[TD([[makeQuery(id+"F0.imprint","IMPRINT",EDGE,{"derivedFrom":subQ1}),1.0]])]});}
            var Q1;
            {var subQ0=sQuery(id+"F0.wireOp",EDGE,"E1.left");var subQ1=sQuery(id+"F0.wireOp",EDGE,"E1.bottom");var subQ2=makeQuery(id+"F0.imprint","INTERSECT",VERTEX,{"derivedFrom":[subQ1,subQ0]});Q1=makeQuery(id+"F0.imprint","IMPRINT",FACE,{"disambiguationData":[TD([[makeQuery(id+"F0.imprint","IMPRINT",EDGE,{"disambiguationData":[TD([[subQ2,-1.0]])],"derivedFrom":subQ1}),1.0]])]});}
            var Q2;
            Q2=makeQuery(id+"F0.imprint","IMPRINT",FACE,{"disambiguationData":[TD([[makeQuery(id+"F0.imprint","IMPRINT",EDGE,{"derivedFrom":sQuery(id+"F0.wireOp",EDGE,"E7")}),-1.0]])]});
            var Q3;
            {var subQ0=sQuery(id+"F0.wireOp",EDGE,"E2.bottom");var subQ1=sQuery(id+"F0.wireOp",EDGE,"E2.left");var subQ2=makeQuery(id+"F0.imprint","INTERSECT",VERTEX,{"derivedFrom":[subQ1,subQ0]});Q3=makeQuery(id+"F0.imprint","IMPRINT",FACE,{"disambiguationData":[TD([[makeQuery(id+"F0.imprint","IMPRINT",EDGE,{"disambiguationData":[TD([[subQ2,-1.0]])],"derivedFrom":subQ1}),1.0]])]});}
            var Q4;
            Q4=makeQuery(id+"F0.imprint","IMPRINT",FACE,{"disambiguationData":[TD([[makeQuery(id+"F0.imprint","IMPRINT",EDGE,{"derivedFrom":sQuery(id+"F0.wireOp",EDGE,"E23.MirrorC")}),1.0]])]});
            var Q5;
            {var subQ0=sQuery(id+"F0.wireOp",EDGE,"E46.MirrorCS");var subQ1=sQuery(id+"F0.wireOp",EDGE,"E34.MirrorCS");var subQ2=makeQuery(id+"F0.imprint","INTERSECT",VERTEX,{"derivedFrom":[subQ1,subQ0]});Q5=makeQuery(id+"F0.imprint","IMPRINT",FACE,{"disambiguationData":[TD([[makeQuery(id+"F0.imprint","IMPRINT",EDGE,{"disambiguationData":[TD([[subQ2,-1.0]])],"derivedFrom":subQ1}),1.0]])]});}
            var Q6;
            Q6=makeQuery(id+"F0.imprint","IMPRINT",FACE,{"disambiguationData":[TD([[makeQuery(id+"F0.imprint","IMPRINT",EDGE,{"derivedFrom":sQuery(id+"F0.wireOp",EDGE,"E24.MirrorC")}),1.0]])]});
            var Q7;
            {var subQ0=sQuery(id+"F0.wireOp",EDGE,"E48.MirrorCS");var subQ1=sQuery(id+"F0.wireOp",EDGE,"E36.MirrorCS");var subQ2=makeQuery(id+"F0.imprint","INTERSECT",VERTEX,{"derivedFrom":[subQ1,subQ0]});Q7=makeQuery(id+"F0.imprint","IMPRINT",FACE,{"disambiguationData":[TD([[makeQuery(id+"F0.imprint","IMPRINT",EDGE,{"disambiguationData":[TD([[subQ2,-1.0]])],"derivedFrom":subQ1}),-1.0]])]});}
            var Q8;
            {var subQ0=sQuery(id+"F0.wireOp",EDGE,"E107.1");Q8=makeQuery(id+"F0.imprint","IMPRINT",FACE,{"disambiguationData":[TD([[makeQuery(id+"F0.imprint","IMPRINT",EDGE,{"derivedFrom":subQ0}),1.0]])]});}
            var Q9;
            Q9=makeQuery(id+"F0.imprint","IMPRINT",FACE,{"disambiguationData":[TD([[makeQuery(id+"F0.imprint","IMPRINT",EDGE,{"derivedFrom":sQuery(id+"F0.wireOp",EDGE,"E170.MirrorC")}),1.0]])]});
            var Q10;
            {var subQ9=sQuery(id+"F0.wireOp",EDGE,"E74");Q10=makeQuery(id+"F0.imprint","IMPRINT",FACE,{"disambiguationData":[TD([[makeQuery(id+"F0.imprint","IMPRINT",EDGE,{"derivedFrom":subQ9}),1.0]])]});}
            var Q11;
            {var subQ4=sQuery(id+"F0.wireOp",EDGE,"E14");Q11=makeQuery(id+"F0.imprint","IMPRINT",FACE,{"disambiguationData":[TD([[makeQuery(id+"F0.imprint","IMPRINT",EDGE,{"derivedFrom":subQ4}),1.0]])]});}
            var Q12;
            {var subQ7=sQuery(id+"F0.wireOp",EDGE,"E100");Q12=makeQuery(id+"F0.imprint","IMPRINT",FACE,{"disambiguationData":[TD([[makeQuery(id+"F0.imprint","IMPRINT",EDGE,{"derivedFrom":subQ7}),1.0]])]});}
            var Q13;
            {var subQ0=sQuery(id+"F0.wireOp",EDGE,"E100");Q13=makeQuery(id+"F0.imprint","IMPRINT",FACE,{"disambiguationData":[TD([[makeQuery(id+"F0.imprint","IMPRINT",EDGE,{"derivedFrom":subQ0}),-1.0]])]});}
            extrude(context, id + "F2", {"entities" : qUnion([Q0, Q1, Q2, Q3, Q4, Q5, Q6, Q7, Q8, Q9, Q10, Q11, Q12, Q13]), "operationType" : NewBodyOperationType.ADD, "depth" : 30 * mm, "offsetDistance" : 25 * mm});
        }
        {
            var Q0;
            Q0=makeQuery(id+"F0.imprint","IMPRINT",FACE,{"disambiguationData":[TD([[makeQuery(id+"F0.imprint","IMPRINT",EDGE,{"derivedFrom":sQuery(id+"F0.wireOp",EDGE,"E21.MirrorCS")}),-1.0]])]});
            var Q1;
            Q1=makeQuery(id+"F0.imprint","IMPRINT",FACE,{"disambiguationData":[TD([[makeQuery(id+"F0.imprint","IMPRINT",EDGE,{"derivedFrom":sQuery(id+"F0.wireOp",EDGE,"E8")}),-1.0]])]});
            extrude(context, id + "F3", {"entities" : qUnion([Q0, Q1]), "operationType" : NewBodyOperationType.ADD, "depth" : 35 * mm, "offsetDistance" : 25 * mm});
        }
        {
            var Q0;
            {var subQ0=sQuery(id+"F0.wireOp",EDGE,"E12.0");var subQ1=sQuery(id+"F0.wireOp",EDGE,"E11.3");var subQ2=makeQuery(id+"F0.imprint","INTERSECT",VERTEX,{"derivedFrom":[subQ1,subQ0]});Q0=makeQuery(id+"F0.imprint","IMPRINT",FACE,{"disambiguationData":[TD([[makeQuery(id+"F0.imprint","IMPRINT",EDGE,{"disambiguationData":[TD([[subQ2,-1.0]])],"derivedFrom":subQ1}),-1.0]])]});}
            var Q1;
            {var subQ3=sQuery(id+"F0.wireOp",EDGE,"E151.MirrorC");var subQ7=sQuery(id+"F0.wireOp",EDGE,"E11.3");var subQ12=makeQuery(id+"F0.imprint","INTERSECT",VERTEX,{"derivedFrom":[subQ7,subQ3]});Q1=makeQuery(id+"F0.imprint","IMPRINT",FACE,{"disambiguationData":[TD([[makeQuery(id+"F0.imprint","IMPRINT",EDGE,{"disambiguationData":[TD([[subQ12,-1.0]])],"derivedFrom":subQ7}),-1.0]])]});}
            var Q2;
            {var subQ0=sQuery(id+"F0.wireOp",EDGE,"E151.MirrorC");var subQ1=sQuery(id+"F0.wireOp",EDGE,"E11.3");var subQ2=makeQuery(id+"F0.imprint","INTERSECT",VERTEX,{"derivedFrom":[subQ1,subQ0]});Q2=makeQuery(id+"F0.imprint","IMPRINT",FACE,{"disambiguationData":[TD([[makeQuery(id+"F0.imprint","IMPRINT",EDGE,{"disambiguationData":[TD([[subQ2,-1.0]])],"derivedFrom":subQ1}),1.0]])]});}
            var Q3;
            {var subQ6=sQuery(id+"F0.wireOp",EDGE,"E12.1");Q3=makeQuery(id+"F0.imprint","IMPRINT",FACE,{"disambiguationData":[TD([[makeQuery(id+"F0.imprint","IMPRINT",EDGE,{"derivedFrom":subQ6}),-1.0]])]});}
            var Q4;
            {var subQ0=sQuery(id+"F0.wireOp",EDGE,"E60");Q4=makeQuery(id+"F0.imprint","IMPRINT",FACE,{"disambiguationData":[TD([[makeQuery(id+"F0.imprint","IMPRINT",EDGE,{"derivedFrom":subQ0}),1.0]])]});}
            var Q5;
            {var subQ7=sQuery(id+"F0.wireOp",EDGE,"E12.1");Q5=makeQuery(id+"F0.imprint","IMPRINT",FACE,{"disambiguationData":[TD([[makeQuery(id+"F0.imprint","IMPRINT",EDGE,{"derivedFrom":subQ7}),1.0]])]});}
            var Q6;
            {var subQ6=sQuery(id+"F0.wireOp",EDGE,"E1.right");Q6=makeQuery(id+"F0.imprint","IMPRINT",FACE,{"disambiguationData":[TD([[makeQuery(id+"F0.imprint","IMPRINT",EDGE,{"derivedFrom":subQ6}),-1.0]])]});}
            var Q7;
            {var subQ0=sQuery(id+"F0.wireOp",EDGE,"E144");var subQ1=sQuery(id+"F0.wireOp",EDGE,"E11.1");var subQ2=makeQuery(id+"F0.imprint","INTERSECT",VERTEX,{"derivedFrom":[subQ1,subQ0]});Q7=makeQuery(id+"F0.imprint","IMPRINT",FACE,{"disambiguationData":[TD([[makeQuery(id+"F0.imprint","IMPRINT",EDGE,{"disambiguationData":[TD([[subQ2,-1.0]])],"derivedFrom":subQ1}),-1.0]])]});}
            var Q8;
            {var subQ3=sQuery(id+"F0.wireOp",EDGE,"E144");var subQ10=sQuery(id+"F0.wireOp",EDGE,"E11.1");var subQ11=makeQuery(id+"F0.imprint","INTERSECT",VERTEX,{"derivedFrom":[subQ10,subQ3]});Q8=makeQuery(id+"F0.imprint","IMPRINT",FACE,{"disambiguationData":[TD([[makeQuery(id+"F0.imprint","IMPRINT",EDGE,{"disambiguationData":[TD([[subQ11,-1.0]])],"derivedFrom":subQ10}),1.0]])]});}
            var Q9;
            {var subQ5=sQuery(id+"F0.wireOp",EDGE,"E13.0");var subQ6=sQuery(id+"F0.wireOp",EDGE,"E11.1");var subQ7=makeQuery(id+"F0.imprint","INTERSECT",VERTEX,{"derivedFrom":[subQ6,subQ5]});Q9=makeQuery(id+"F0.imprint","IMPRINT",FACE,{"disambiguationData":[TD([[makeQuery(id+"F0.imprint","IMPRINT",EDGE,{"disambiguationData":[TD([[subQ7,-1.0]])],"derivedFrom":subQ6}),1.0]])]});}
            var Q10;
            {var subQ0=sQuery(id+"F0.wireOp",EDGE,"E63");Q10=makeQuery(id+"F0.imprint","IMPRINT",FACE,{"disambiguationData":[TD([[makeQuery(id+"F0.imprint","IMPRINT",EDGE,{"derivedFrom":subQ0}),1.0]])]});}
            var Q11;
            {var subQ2=sQuery(id+"F0.wireOp",EDGE,"E62");Q11=makeQuery(id+"F0.imprint","IMPRINT",FACE,{"disambiguationData":[TD([[makeQuery(id+"F0.imprint","IMPRINT",EDGE,{"derivedFrom":subQ2}),1.0]])]});}
            var Q12;
            {var subQ0=sQuery(id+"F0.wireOp",EDGE,"E62");Q12=makeQuery(id+"F0.imprint","IMPRINT",FACE,{"disambiguationData":[TD([[makeQuery(id+"F0.imprint","IMPRINT",EDGE,{"derivedFrom":subQ0}),-1.0]])]});}
            var Q13;
            {var subQ1=sQuery(id+"F0.wireOp",EDGE,"E31.MirrorCS");Q13=makeQuery(id+"F0.imprint","IMPRINT",FACE,{"disambiguationData":[TD([[makeQuery(id+"F0.imprint","IMPRINT",EDGE,{"derivedFrom":subQ1}),1.0]])]});}
            var Q14;
            {var subQ0=sQuery(id+"F0.wireOp",EDGE,"E145");var subQ1=sQuery(id+"F0.wireOp",EDGE,"E11.1");var subQ2=makeQuery(id+"F0.imprint","INTERSECT",VERTEX,{"derivedFrom":[subQ1,subQ0]});Q14=makeQuery(id+"F0.imprint","IMPRINT",FACE,{"disambiguationData":[TD([[makeQuery(id+"F0.imprint","IMPRINT",EDGE,{"disambiguationData":[TD([[subQ2,1.0]])],"derivedFrom":subQ1}),-1.0]])]});}
            var Q15;
            {var subQ3=sQuery(id+"F0.wireOp",EDGE,"E145");var subQ10=sQuery(id+"F0.wireOp",EDGE,"E11.1");var subQ11=makeQuery(id+"F0.imprint","INTERSECT",VERTEX,{"derivedFrom":[subQ10,subQ3]});Q15=makeQuery(id+"F0.imprint","IMPRINT",FACE,{"disambiguationData":[TD([[makeQuery(id+"F0.imprint","IMPRINT",EDGE,{"disambiguationData":[TD([[subQ11,1.0]])],"derivedFrom":subQ10}),1.0]])]});}
            var Q16;
            Q16=makeQuery(id+"F0.imprint","IMPRINT",FACE,{"disambiguationData":[TD([[makeQuery(id+"F0.imprint","IMPRINT",EDGE,{"derivedFrom":sQuery(id+"F0.wireOp",EDGE,"E21.MirrorCS")}),1.0]])]});
            var Q17;
            {var subQ0=sQuery(id+"F0.wireOp",EDGE,"E153.MirrorC");var subQ1=sQuery(id+"F0.wireOp",EDGE,"E11.3");var subQ2=makeQuery(id+"F0.imprint","INTERSECT",VERTEX,{"derivedFrom":[subQ1,subQ0]});Q17=makeQuery(id+"F0.imprint","IMPRINT",FACE,{"disambiguationData":[TD([[makeQuery(id+"F0.imprint","IMPRINT",EDGE,{"disambiguationData":[TD([[subQ2,1.0]])],"derivedFrom":subQ1}),1.0]])]});}
            var Q18;
            {var subQ3=sQuery(id+"F0.wireOp",EDGE,"E153.MirrorC");var subQ5=sQuery(id+"F0.wireOp",EDGE,"E11.3");var subQ6=makeQuery(id+"F0.imprint","INTERSECT",VERTEX,{"derivedFrom":[subQ5,subQ3]});Q18=makeQuery(id+"F0.imprint","IMPRINT",FACE,{"disambiguationData":[TD([[makeQuery(id+"F0.imprint","IMPRINT",EDGE,{"disambiguationData":[TD([[subQ6,1.0]])],"derivedFrom":subQ5}),-1.0]])]});}
            var Q19;
            {var subQ5=sQuery(id+"F0.wireOp",EDGE,"E25.MirrorCS");Q19=makeQuery(id+"F0.imprint","IMPRINT",FACE,{"disambiguationData":[TD([[makeQuery(id+"F0.imprint","IMPRINT",EDGE,{"derivedFrom":subQ5}),-1.0]])]});}
            var Q20;
            {var subQ0=sQuery(id+"F0.wireOp",EDGE,"E61");Q20=makeQuery(id+"F0.imprint","IMPRINT",FACE,{"disambiguationData":[TD([[makeQuery(id+"F0.imprint","IMPRINT",EDGE,{"derivedFrom":subQ0}),-1.0]])]});}
            var Q21;
            {var subQ0=sQuery(id+"F0.wireOp",EDGE,"E60");Q21=makeQuery(id+"F0.imprint","IMPRINT",FACE,{"disambiguationData":[TD([[makeQuery(id+"F0.imprint","IMPRINT",EDGE,{"derivedFrom":subQ0}),-1.0]])]});}
            var Q22;
            {var subQ5=sQuery(id+"F0.wireOp",EDGE,"E17");Q22=makeQuery(id+"F0.imprint","IMPRINT",FACE,{"disambiguationData":[TD([[makeQuery(id+"F0.imprint","IMPRINT",EDGE,{"derivedFrom":subQ5}),-1.0]])]});}
            var Q23;
            {var subQ5=sQuery(id+"F0.wireOp",EDGE,"E17");Q23=makeQuery(id+"F0.imprint","IMPRINT",FACE,{"disambiguationData":[TD([[makeQuery(id+"F0.imprint","IMPRINT",EDGE,{"derivedFrom":subQ5}),1.0]])]});}
            var Q24;
            {var subQ1=sQuery(id+"F0.wireOp",EDGE,"E20");Q24=makeQuery(id+"F0.imprint","IMPRINT",FACE,{"disambiguationData":[TD([[makeQuery(id+"F0.imprint","IMPRINT",EDGE,{"derivedFrom":subQ1}),1.0]])]});}
            var Q25;
            {var subQ1=sQuery(id+"F0.wireOp",EDGE,"E14");Q25=makeQuery(id+"F0.imprint","IMPRINT",FACE,{"disambiguationData":[TD([[makeQuery(id+"F0.imprint","IMPRINT",EDGE,{"derivedFrom":subQ1}),-1.0]])]});}
            extrude(context, id + "F4", {"entities" : qUnion([Q0, Q1, Q2, Q3, Q4, Q5, Q6, Q7, Q8, Q9, Q10, Q11, Q12, Q13, Q14, Q15, Q16, Q17, Q18, Q19, Q20, Q21, Q22, Q23, Q24, Q25]), "operationType" : NewBodyOperationType.ADD, "depth" : 40 * mm, "offsetDistance" : 25 * mm});
        }
        {
            var Q0;
            Q0=makeQuery(id+"F4.opExtrude","CAP_EDGE",EDGE,{"disambiguationData":[OSD([sQuery(id+"F0.wireOp",EDGE,"E165.MirrorC")])],"isStart":false});
            var Q1;
            Q1=makeQuery(id+"F4.opExtrude","CAP_EDGE",EDGE,{"disambiguationData":[OSD([sQuery(id+"F0.wireOp",EDGE,"E164.MirrorC")])],"isStart":false});
            var Q2;
            Q2=makeQuery(id+"F1.opExtrude","CAP_EDGE",EDGE,{"disambiguationData":[OSD([sQuery(id+"F0.wireOp",EDGE,"E162")])],"isStart":false});
            var Q3;
            Q3=makeQuery(id+"F1.opExtrude","CAP_EDGE",EDGE,{"disambiguationData":[OSD([sQuery(id+"F0.wireOp",EDGE,"E166.MirrorC")])],"isStart":false});
            var Q4;
            Q4=makeQuery(id+"F4.opExtrude","CAP_EDGE",EDGE,{"disambiguationData":[OSD([sQuery(id+"F0.wireOp",EDGE,"E167.MirrorC")])],"isStart":false});
            var Q5;
            Q5=makeQuery(id+"F4.opExtrude","CAP_EDGE",EDGE,{"disambiguationData":[OSD([sQuery(id+"F0.wireOp",EDGE,"E163")])],"isStart":false});
            var Q6;
            Q6=makeQuery(id+"F4.opExtrude","CAP_EDGE",EDGE,{"disambiguationData":[OSD([sQuery(id+"F0.wireOp",EDGE,"E147")])],"isStart":false});
            var Q7;
            Q7=makeQuery(id+"F4.opExtrude","CAP_EDGE",EDGE,{"disambiguationData":[OSD([sQuery(id+"F0.wireOp",EDGE,"E156")])],"isStart":false});
            var Q8;
            Q8=makeQuery(id+"F2.opExtrude","CAP_EDGE",EDGE,{"disambiguationData":[OSD([sQuery(id+"F0.wireOp",EDGE,"E168")])],"isStart":false});
            var Q9;
            Q9=makeQuery(id+"F2.opExtrude","CAP_EDGE",EDGE,{"disambiguationData":[OSD([sQuery(id+"F0.wireOp",EDGE,"E169.MirrorC")])],"isStart":false});
            var Q10;
            Q10=makeQuery(id+"F4.opExtrude","CAP_EDGE",EDGE,{"disambiguationData":[OSD([sQuery(id+"F0.wireOp",EDGE,"E159.MirrorC")])],"isStart":false});
            var Q11;
            Q11=makeQuery(id+"F4.opExtrude","CAP_EDGE",EDGE,{"disambiguationData":[OSD([sQuery(id+"F0.wireOp",EDGE,"E150.MirrorC")])],"isStart":false});
            var Q12;
            Q12=makeQuery(id+"F2.opExtrude","CAP_EDGE",EDGE,{"disambiguationData":[OSD([sQuery(id+"F0.wireOp",EDGE,"E171.MirrorC")])],"isStart":false});
            var Q13;
            Q13=makeQuery(id+"F2.opExtrude","CAP_EDGE",EDGE,{"disambiguationData":[OSD([sQuery(id+"F0.wireOp",EDGE,"E170.MirrorC")])],"isStart":false});
            var Q14;
            Q14=makeQuery(id+"F4.opExtrude","CAP_EDGE",EDGE,{"disambiguationData":[OSD([sQuery(id+"F0.wireOp",EDGE,"E161.MirrorC")])],"isStart":false});
            var Q15;
            Q15=makeQuery(id+"F4.opExtrude","CAP_EDGE",EDGE,{"disambiguationData":[OSD([sQuery(id+"F0.wireOp",EDGE,"E146")])],"isStart":false});
            var Q16;
            Q16=makeQuery(id+"F4.opExtrude","CAP_EDGE",EDGE,{"disambiguationData":[OSD([sQuery(id+"F0.wireOp",EDGE,"E160.MirrorC")])],"isStart":false});
            var Q17;
            Q17=makeQuery(id+"F4.opExtrude","CAP_EDGE",EDGE,{"disambiguationData":[OSD([sQuery(id+"F0.wireOp",EDGE,"E152.MirrorC")])],"isStart":false});
            fillet(context, id + "F5", {"entities" : qUnion([Q0, Q1, Q2, Q3, Q4, Q5, Q6, Q7, Q8, Q9, Q10, Q11, Q12, Q13, Q14, Q15, Q16, Q17]), "radius" : 1.98 * mm, "tangentPropagation" : true, "allowEdgeOverflow" : false});
        }
    });
